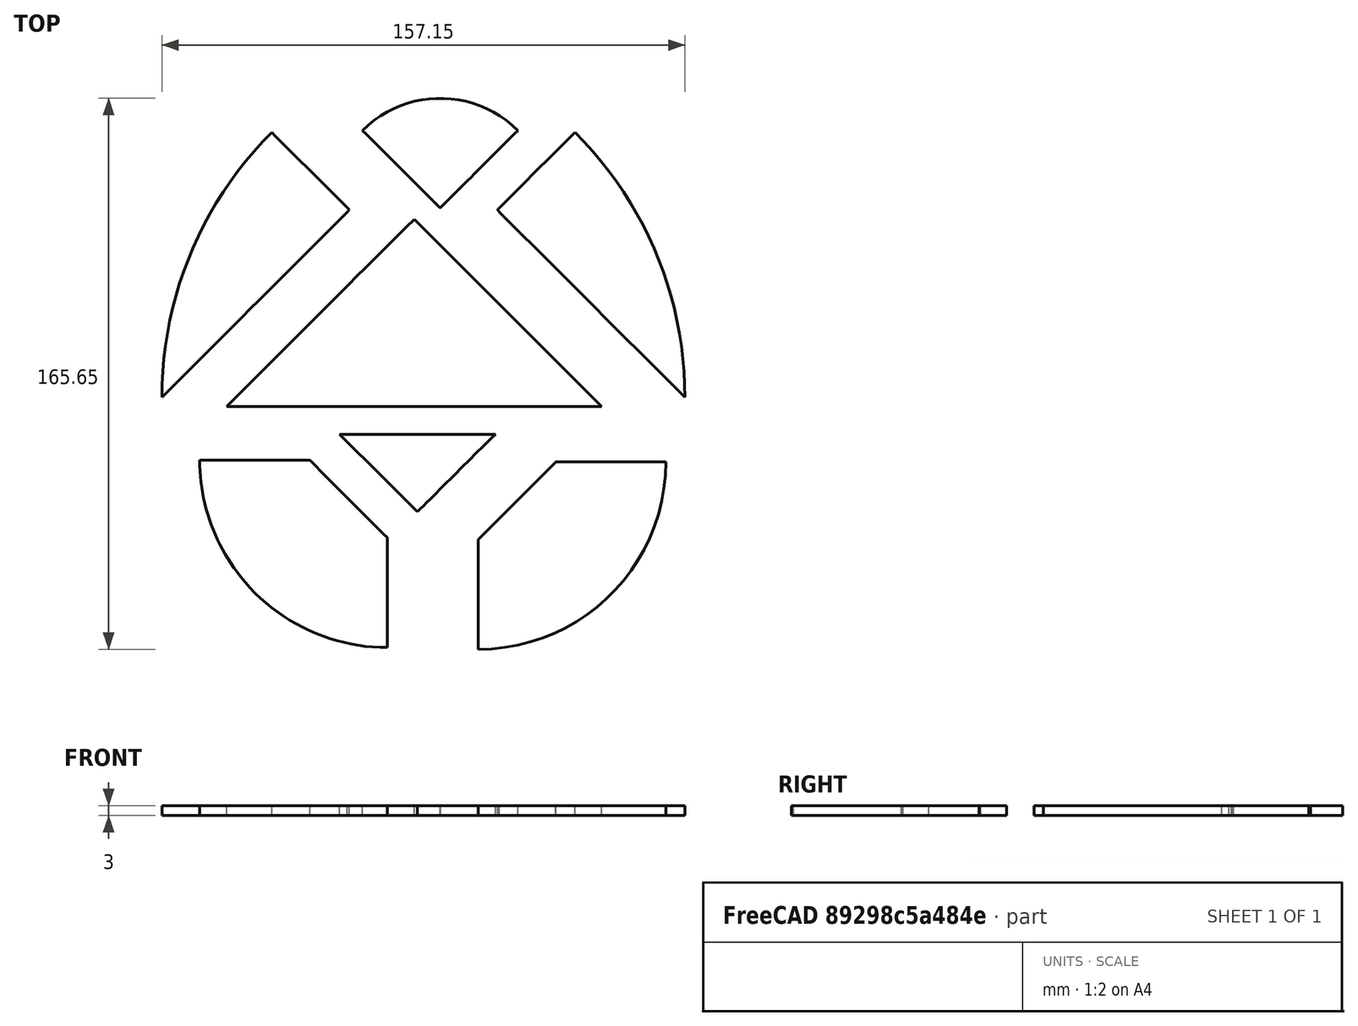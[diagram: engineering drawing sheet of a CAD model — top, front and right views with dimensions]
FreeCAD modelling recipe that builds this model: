
FCSTD DOCUMENT  (FreeCAD 0.17R13509 (Git))
Label: Puzzle_Huevo
License: CreativeCommons Attribution-ShareAlike
LicenseURL: http://creativecommons.org/licenses/by-sa/4.0/
objects: Part::Feature×7, Part::Extrusion×7
note: 14 computed .brp shape members not serialized (recipe doc carries the construction recipe); baked Part::Feature solids carry a one-line shape summary decoded from their .brp

FEATURE [Part::Feature] path6079
  shape: bbox 56.35 x 56.35 x 4.907e-07 mm, 0 faces, 0 solids (baked)
FEATURE [Part::Feature] path6089
  shape: bbox 56.4 x 56.48 x 4.907e-07 mm, 0 faces, 0 solids (baked)
FEATURE [Part::Feature] path6101
  shape: bbox 46.75 x 23.34 x 4.907e-07 mm, 0 faces, 0 solids (baked)
FEATURE [Part::Feature] path6120
  shape: bbox 56.29 x 79.69 x 2e-07 mm, 0 faces, 0 solids (baked)
FEATURE [Part::Feature] path6123
  shape: bbox 56.29 x 79.69 x 2e-07 mm, 0 faces, 0 solids (baked)
FEATURE [Part::Feature] path6134
  shape: bbox 46.68 x 34.73 x 4.907e-07 mm, 0 faces, 0 solids (baked)
FEATURE [Part::Feature] path6140
  shape: bbox 112.7 x 56.31 x 4.907e-07 mm, 0 faces, 0 solids (baked)
FEATURE [Part::Extrusion] Extrude  label="Extrude1"
  Base = -> path6079
  Dir = (0,0,1)
  DirMode = 0
  FaceMakerClass = Part::FaceMakerBullseye
  LengthFwd = 3
  LengthRev = 0
  Solid = true
  Symmetric = false
FEATURE [Part::Extrusion] Extrude001  label="Extrude2"
  Base = -> path6089
  Dir = (0,0,1)
  DirMode = 0
  FaceMakerClass = Part::FaceMakerBullseye
  LengthFwd = 3
  LengthRev = 0
  Solid = true
  Symmetric = false
FEATURE [Part::Extrusion] Extrude002  label="Extrude3"
  Base = -> path6101
  Dir = (0,0,1)
  DirMode = 0
  FaceMakerClass = Part::FaceMakerBullseye
  LengthFwd = 3
  LengthRev = 0
  Solid = true
  Symmetric = false
FEATURE [Part::Extrusion] Extrude003  label="Extrude4"
  Base = -> path6120
  Dir = (0,0,1)
  DirMode = 0
  FaceMakerClass = Part::FaceMakerBullseye
  LengthFwd = 3
  LengthRev = 0
  Solid = true
  Symmetric = false
FEATURE [Part::Extrusion] Extrude004  label="Extrude5"
  Base = -> path6123
  Dir = (0,0,1)
  DirMode = 0
  FaceMakerClass = Part::FaceMakerBullseye
  LengthFwd = 3
  LengthRev = 0
  Solid = true
  Symmetric = false
FEATURE [Part::Extrusion] Extrude005  label="Extrude6"
  Base = -> path6134
  Dir = (0,0,1)
  DirMode = 0
  FaceMakerClass = Part::FaceMakerBullseye
  LengthFwd = 3
  LengthRev = 0
  Solid = true
  Symmetric = false
FEATURE [Part::Extrusion] Extrude006  label="Extrude7"
  Base = -> path6140
  Dir = (0,0,1)
  DirMode = 0
  FaceMakerClass = Part::FaceMakerBullseye
  LengthFwd = 3
  LengthRev = 0
  Solid = true
  Symmetric = false
